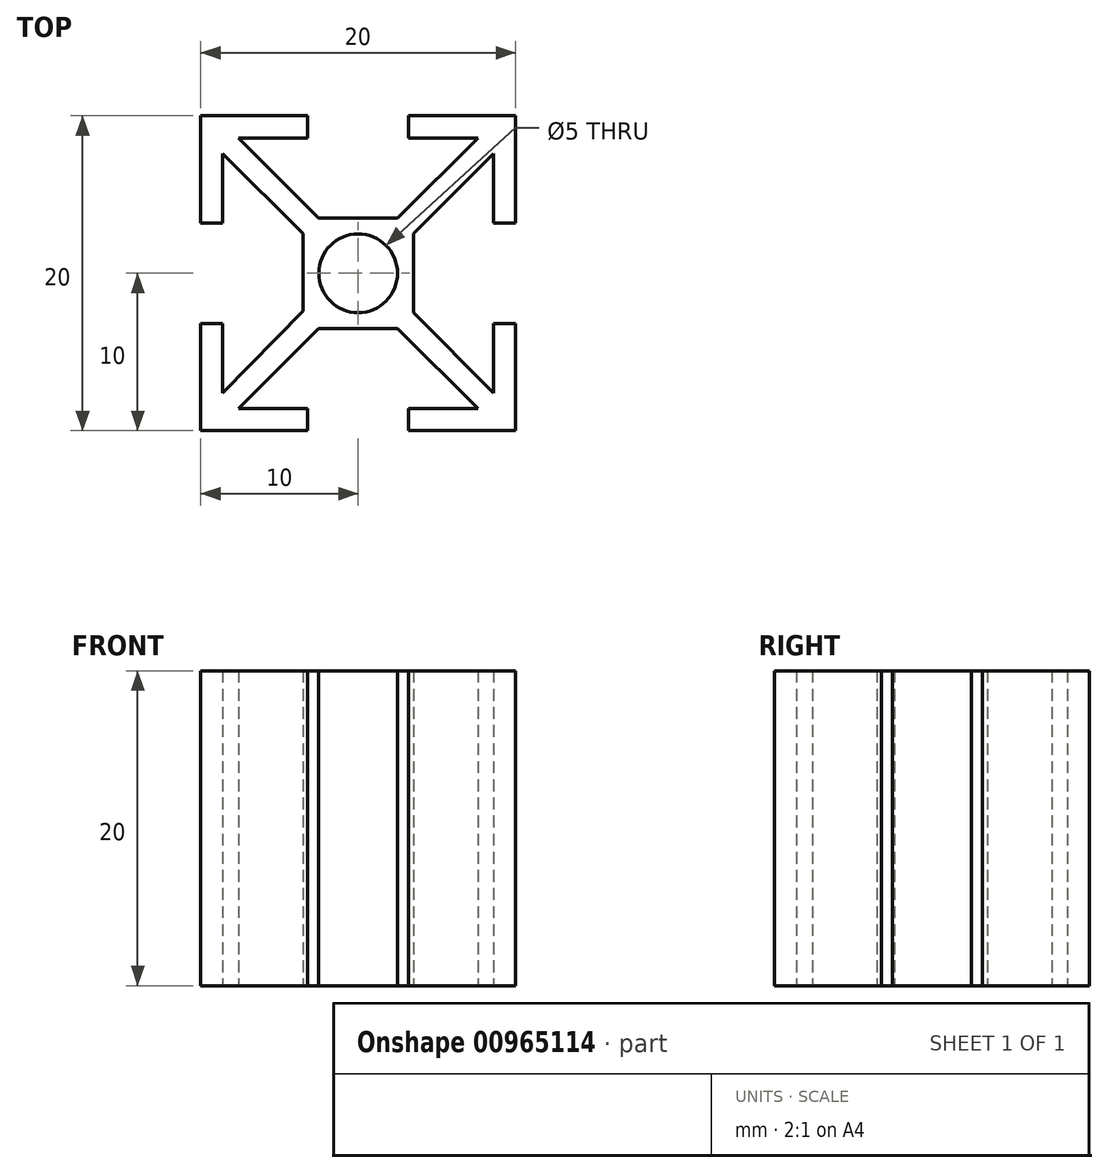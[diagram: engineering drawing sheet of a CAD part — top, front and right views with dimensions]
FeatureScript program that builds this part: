
annotation { "Feature Type Name" : "Feature", "Feature Type Description" : "" }
export const myFeature = defineFeature(function(context is Context, id is Id, definition is map)
    precondition{}
    {
        {
            var Q0;
            Q0=qCreatedBy(makeId("Top.planeOp"),FACE);
            var sketch = newSketch(context, id + "F0", { "sketchPlane" : qUnion([Q0])});
            skCircle(sketch, "E0", {"center": v(10, 10) * mm, "radius": 2.5 * mm});
            skLineSegment(sketch, "E1", {"start": v(0, 0) * mm, "end": v(10, 10) * mm, "construction": true});
            skLineSegment(sketch, "E2", {"start": v(1.4, 2.39) * mm, "end": v(1.4, 6.8) * mm});
            skLineSegment(sketch, "E3", {"start": v(1.4, 6.8) * mm, "end": v(0, 6.8) * mm});
            skLineSegment(sketch, "E4", {"start": v(0, 6.8) * mm, "end": v(0, 0) * mm});
            skLineSegment(sketch, "E5", {"start": v(7.49, 6.5) * mm, "end": v(2.39, 1.4) * mm});
            skLineSegment(sketch, "E6", {"start": v(2.39, 1.4) * mm, "end": v(6.8, 1.4) * mm});
            skLineSegment(sketch, "E7", {"start": v(6.8, 1.4) * mm, "end": v(6.8, 0) * mm});
            skLineSegment(sketch, "E8", {"start": v(6.8, 0) * mm, "end": v(0, 0) * mm});
            skLineSegment(sketch, "E9", {"start": v(10, 10) * mm, "end": v(20, 20) * mm, "construction": true});
            skLineSegment(sketch, "E10", {"start": v(10, 10) * mm, "end": v(0, 20) * mm, "construction": true});
            skLineSegment(sketch, "E11", {"start": v(10, 10) * mm, "end": v(20, 0) * mm, "construction": true});
            skLineSegment(sketch, "E12", {"start": v(1.4, 17.61) * mm, "end": v(6.5, 12.51) * mm});
            skLineSegment(sketch, "E13", {"start": v(1.4, 17.61) * mm, "end": v(1.4, 13.2) * mm});
            skLineSegment(sketch, "E14", {"start": v(1.4, 13.2) * mm, "end": v(0, 13.2) * mm});
            skLineSegment(sketch, "E15", {"start": v(0, 13.2) * mm, "end": v(0, 20) * mm});
            skLineSegment(sketch, "E16", {"start": v(7.49, 13.5) * mm, "end": v(2.39, 18.6) * mm});
            skLineSegment(sketch, "E17", {"start": v(2.39, 18.6) * mm, "end": v(6.8, 18.6) * mm});
            skLineSegment(sketch, "E18", {"start": v(6.8, 18.6) * mm, "end": v(6.8, 20) * mm});
            skLineSegment(sketch, "E19", {"start": v(6.8, 20) * mm, "end": v(0, 20) * mm});
            skLineSegment(sketch, "E20", {"start": v(12.51, 13.5) * mm, "end": v(17.61, 18.6) * mm});
            skLineSegment(sketch, "E21", {"start": v(17.61, 18.6) * mm, "end": v(13.2, 18.6) * mm});
            skLineSegment(sketch, "E22", {"start": v(13.2, 18.6) * mm, "end": v(13.2, 20) * mm});
            skLineSegment(sketch, "E23", {"start": v(13.2, 20) * mm, "end": v(20, 20) * mm});
            skLineSegment(sketch, "E24", {"start": v(13.5, 12.51) * mm, "end": v(18.6, 17.61) * mm});
            skLineSegment(sketch, "E25", {"start": v(18.6, 17.61) * mm, "end": v(18.6, 13.2) * mm});
            skLineSegment(sketch, "E26", {"start": v(18.6, 13.2) * mm, "end": v(20, 13.2) * mm});
            skLineSegment(sketch, "E27", {"start": v(20, 13.2) * mm, "end": v(20, 20) * mm});
            skLineSegment(sketch, "E28", {"start": v(18.6, 2.39) * mm, "end": v(18.6, 6.8) * mm});
            skLineSegment(sketch, "E29", {"start": v(18.6, 6.8) * mm, "end": v(20, 6.8) * mm});
            skLineSegment(sketch, "E30", {"start": v(20, 6.8) * mm, "end": v(20, 0) * mm});
            skLineSegment(sketch, "E31", {"start": v(12.51, 6.5) * mm, "end": v(17.61, 1.4) * mm});
            skLineSegment(sketch, "E32", {"start": v(17.61, 1.4) * mm, "end": v(13.2, 1.4) * mm});
            skLineSegment(sketch, "E33", {"start": v(13.2, 1.4) * mm, "end": v(13.2, 0) * mm});
            skLineSegment(sketch, "E34", {"start": v(13.2, 0) * mm, "end": v(20, 0) * mm});
            skLineSegment(sketch, "E35", {"start": v(12.51, 6.5) * mm, "end": v(7.49, 6.5) * mm});
            skLineSegment(sketch, "E36", {"start": v(7.49, 13.5) * mm, "end": v(12.51, 13.5) * mm});
            skLineSegment(sketch, "E37", {"start": v(10, 10) * mm, "end": v(10, 0) * mm, "construction": true});
            skLineSegment(sketch, "E38", {"start": v(10, 10) * mm, "end": v(18.77, 10) * mm, "construction": true});
            skLineSegment(sketch, "E39", {"start": v(10, 10) * mm, "end": v(10, 20.74) * mm, "construction": true});
            skLineSegment(sketch, "E40", {"start": v(10, 10) * mm, "end": v(0, 10) * mm, "construction": true});
            skLineSegment(sketch, "E41.bottom", {"start": v(0, 0) * mm, "end": v(20, 0) * mm, "construction": true});
            skLineSegment(sketch, "E41.top", {"start": v(0, 20) * mm, "end": v(20, 20) * mm, "construction": true});
            skLineSegment(sketch, "E41.left", {"start": v(0, 0) * mm, "end": v(0, 20) * mm, "construction": true});
            skLineSegment(sketch, "E41.right", {"start": v(20, 0) * mm, "end": v(20, 20) * mm, "construction": true});
            skLineSegment(sketch, "E42", {"start": v(18.6, 2.39) * mm, "end": v(13.5, 7.49) * mm});
            skLineSegment(sketch, "E43", {"start": v(13.5, 7.49) * mm, "end": v(13.5, 12.51) * mm});
            skLineSegment(sketch, "E44", {"start": v(1.4, 2.39) * mm, "end": v(6.5, 7.62) * mm});
            skLineSegment(sketch, "E45", {"start": v(6.5, 7.62) * mm, "end": v(6.5, 12.51) * mm});
            skSolve(sketch);
        }
        {
            var Q0;
            Q0=makeQuery(id+"F0.imprint","IMPRINT",FACE,{"disambiguationData":[TD([[makeQuery(id+"F0.imprint","IMPRINT",EDGE,{"derivedFrom":sQuery(id+"F0.wireOp",EDGE,"E0")}),-1.0]])]});
            extrude(context, id + "F1", {"entities" : qUnion([Q0]), "depth" : 20 * mm, "offsetDistance" : 25 * mm});
        }
    });
